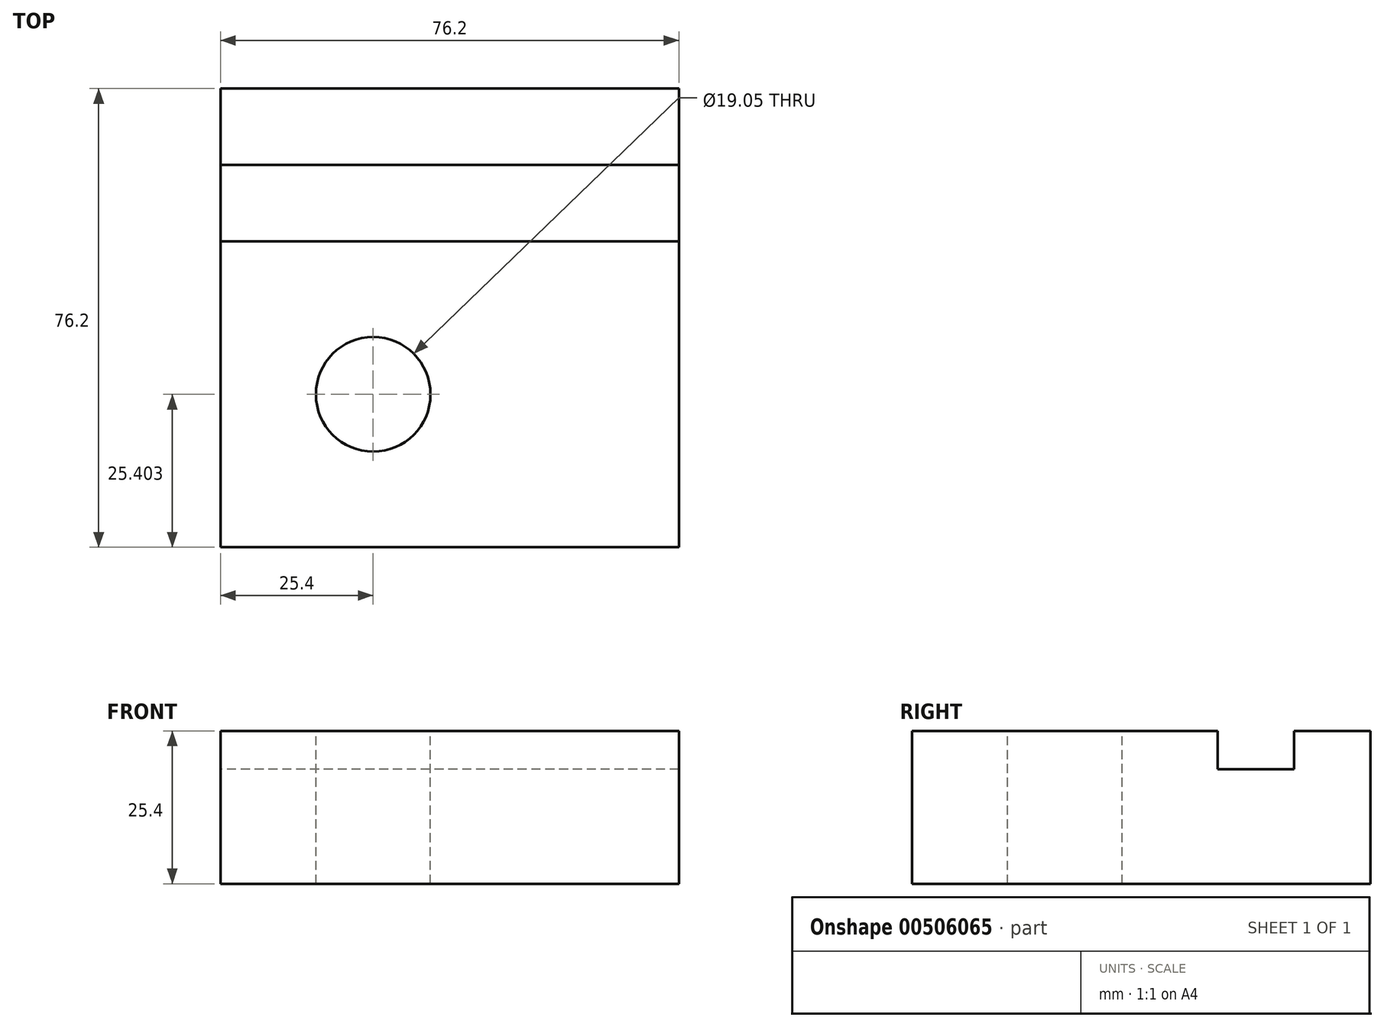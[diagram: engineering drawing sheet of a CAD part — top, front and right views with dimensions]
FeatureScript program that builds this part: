
annotation { "Feature Type Name" : "Feature", "Feature Type Description" : "" }
export const myFeature = defineFeature(function(context is Context, id is Id, definition is map)
    precondition{}
    {
        {
            var Q0;
            Q0=qCreatedBy(makeId("Right.planeOp"),FACE);
            var sketch = newSketch(context, id + "F0", { "sketchPlane" : qUnion([Q0])});
            skLineSegment(sketch, "E0", {"start": v(-41.39, 0) * mm, "end": v(34.81, 0) * mm});
            skLineSegment(sketch, "E1", {"start": v(34.81, 0) * mm, "end": v(34.81, 25.4) * mm});
            skLineSegment(sketch, "E2", {"start": v(34.81, 25.4) * mm, "end": v(22.11, 25.4) * mm});
            skLineSegment(sketch, "E3", {"start": v(22.11, 25.4) * mm, "end": v(22.11, 19.05) * mm});
            skLineSegment(sketch, "E4", {"start": v(22.11, 19.05) * mm, "end": v(9.41, 19.05) * mm});
            skLineSegment(sketch, "E5", {"start": v(9.41, 19.05) * mm, "end": v(9.41, 25.4) * mm});
            skLineSegment(sketch, "E6", {"start": v(9.41, 25.4) * mm, "end": v(-41.39, 25.4) * mm});
            skLineSegment(sketch, "E7", {"start": v(-41.39, 25.4) * mm, "end": v(-41.39, 0) * mm});
            skSolve(sketch);
        }
        {
            var Q0;
            Q0 = qSketchRegion(id + "F0", true);
            extrude(context, id + "F1", {"entities" : qUnion([Q0]), "depth" : 76.2 * mm});
        }
        {
            var Q0;
            Q0=makeQuery(id+"F1.opExtrude","SWEPT_FACE",FACE,{"disambiguationData":[OSD([sQuery(id+"F0.wireOp",EDGE,"E6")])]});
            var sketch = newSketch(context, id + "F2", { "sketchPlane" : qUnion([Q0])});
            skCircle(sketch, "E8", {"center": v(25.4, -15.99) * mm, "radius": 9.53 * mm});
            skSolve(sketch);
        }
        {
            var Q0;
            Q0=makeQuery(id+"F2.imprint","IMPRINT",FACE,{"disambiguationData":[TD([[makeQuery(id+"F2.imprint","IMPRINT",EDGE,{"derivedFrom":sQuery(id+"F2.wireOp",EDGE,"E8")}),1.0]])]});
            extrude(context, id + "F3", {"entities" : qUnion([Q0]), "operationType" : NewBodyOperationType.REMOVE, "oppositeDirection" : true, "depth" : 25.4 * mm});
        }
    });
